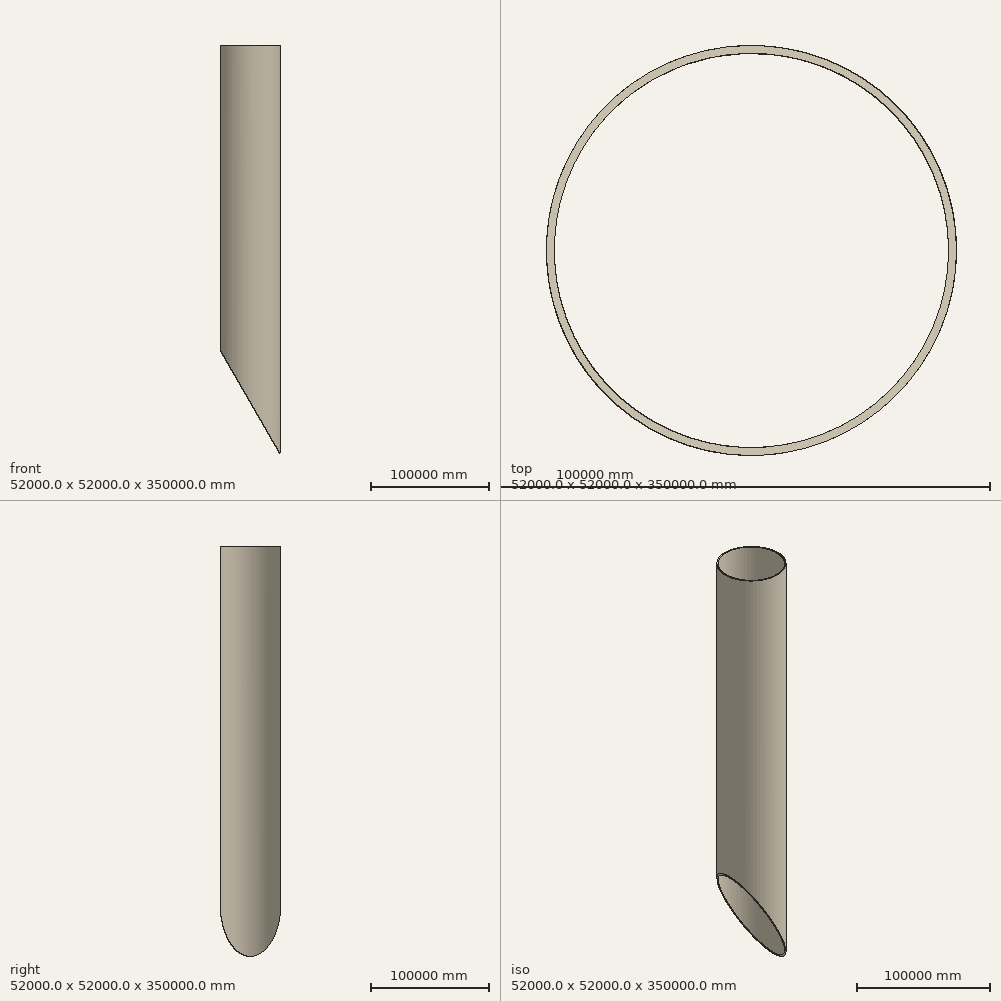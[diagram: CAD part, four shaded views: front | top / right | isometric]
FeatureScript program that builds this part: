
annotation { "Feature Type Name" : "Feature", "Feature Type Description" : "" }
export const myFeature = defineFeature(function(context is Context, id is Id, definition is map)
    precondition{}
    {
        {
            var Q0;
            Q0=qCreatedBy(makeId("Top.planeOp"),FACE);
            var sketch = newSketch(context, id + "F0", { "sketchPlane" : qUnion([Q0])});
            skCircle(sketch, "E0", {"center": v(0, 0) * mm, "radius": 26000 * mm});
            skCircle(sketch, "E1", {"center": v(0, 0) * mm, "radius": 25000 * mm});
            skSolve(sketch);
        }
        {
            var Q0;
            Q0 = qSketchRegion(id + "F0", true);
            extrude(context, id + "F1", {"entities" : qUnion([Q0]), "depth" : 350000 * mm, "offsetDistance" : 25 * mm});
        }
        {
            var Q0;
            Q0=qCreatedBy(makeId("Top.planeOp"),FACE);
            var sketch = newSketch(context, id + "F2", { "sketchPlane" : qUnion([Q0])});
            skLineSegment(sketch, "E2", {"start": v(26000, -35660.13) * mm, "end": v(26000, 33636.97) * mm});
            skSolve(sketch);
        }
        {
            var Q0;
            Q0 = qBodyType(qCreatedBy(id + "F2" ,EDGE), BodyType.WIRE);
            cPlane(context, id + "F3", {"entities" : qUnion([Q0]), "cplaneType" : CPlaneType.LINE_ANGLE, "offset" : 25 * mm, "angle" : 60 * degree, "width" : 150 * mm, "height" : 150 * mm});
        }
        {
            var Q0;
            Q0=qCreatedBy(id+"F3.planeOp",FACE);
            var sketch = newSketch(context, id + "F4", { "sketchPlane" : qUnion([Q0])});
            skLineSegment(sketch, "E3.bottom", {"start": v(54202.16, 98020.07) * mm, "end": v(-39899.17, 98020.07) * mm});
            skLineSegment(sketch, "E3.top", {"start": v(54202.16, -29496.1) * mm, "end": v(-39899.17, -29496.1) * mm});
            skLineSegment(sketch, "E3.left", {"start": v(54202.16, 98020.07) * mm, "end": v(54202.16, -29496.1) * mm});
            skLineSegment(sketch, "E3.right", {"start": v(-39899.17, 98020.07) * mm, "end": v(-39899.17, -29496.1) * mm});
            skSolve(sketch);
        }
        {
            var Q0;
            Q0 = qSketchRegion(id + "F4", true);
            extrude(context, id + "F5", {"entities" : qUnion([Q0]), "operationType" : NewBodyOperationType.REMOVE, "oppositeDirection" : true, "depth" : 55000 * mm, "offsetDistance" : 25 * mm});
        }
    });
